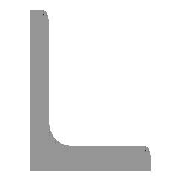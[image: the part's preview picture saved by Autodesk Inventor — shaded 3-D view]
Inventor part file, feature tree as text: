
AUTODESK INVENTOR PART (.ipt)
format: ipt  version: 2023.5 (Build 275446000, 446)  size: 136,192 bytes
history: native  units: mm (DEFAULTED — no unit token found)
features: other x3, sketch x2, hole x1, plane x1, projected_geometry x1
ambient origin geometry x8: Origin, YZ Plane, XZ Plane, XY Plane, X Axis, Y Axis, Z Axis, Center Point
bodies: Solid1 (feature_tree), Body (feature_tree)
feature tree (8):
  other  "Driven Length"
  other  "Start plane"
  other  "End plane"
  hole  "Hole1"  [1 undecoded]
  sketch  "Sketch3"  dims[d0=25.4mm d1=25.4mm]
  plane  "Work Plane3"
  sketch  "Sketch5"  dims[d2=3.175mm d3=3.175mm d4=50.8mm d5=0.0mm d10=0.0mm d11=0.0mm d12=-0.0mm d13=50.8mm d14=3.302mm d15=1.524mm d16=90.0deg d17=50.8mm d18=25.4mm d19=5.1054mm d20=9.652mm d21=9.779mm d22=6.35mm d23=14.3117mm d24=25.4mm d25=20.594885mm]
  projected_geometry  "Projected Loop2"
note: 1 required parameter value undecoded (feature->parameter linkage not recoverable at this tier; creation-order binding heuristic only, values carry confidence <= 0.55)
